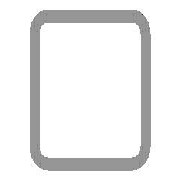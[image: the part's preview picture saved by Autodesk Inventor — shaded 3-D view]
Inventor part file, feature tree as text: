
AUTODESK INVENTOR PART (.ipt)
format: ipt  version: 2024.2 (Build 282272000, 272)  size: 129,024 bytes
history: native  units: mm (DEFAULTED — no unit token found)
features: other x4, sketch x1, plane x1
ambient origin geometry x8: Origin, YZ Plane, XZ Plane, XY Plane, X Axis, Y Axis, Z Axis, Center Point
bodies: Solid1 (feature_tree), Body (feature_tree)
feature tree (6):
  parser-record x1  (decoder bookkeeping rows leaked as tree rows — omitted from the tree; the rows remain in map.json)
  other  "Driven Length"
  other  "Start Plane"
  other  "End Plane"
  sketch  "Sketch3"  dims[d3=2350.0mm d4=0.0mm d7=6.0mm d9=50.0mm d11=50.0mm d12=3.0mm d13=-0.0mm d14=2350.0mm d15=25.0mm d16=25.0mm d17=90.0deg d18=2350.0mm]
  plane  "Work Plane3"
